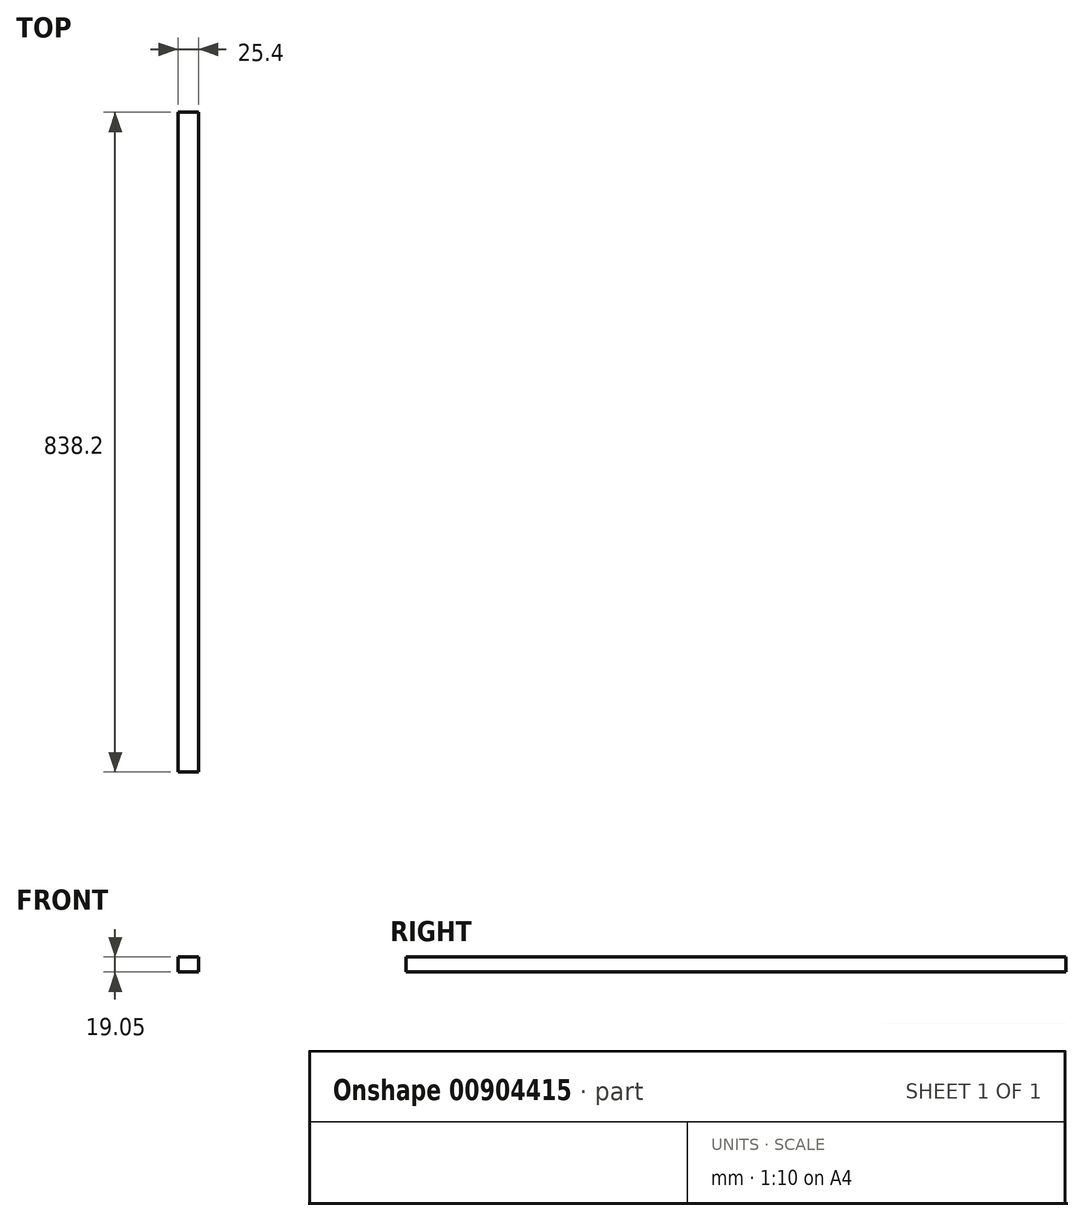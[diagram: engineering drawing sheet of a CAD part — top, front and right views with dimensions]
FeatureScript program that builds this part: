
annotation { "Feature Type Name" : "Feature", "Feature Type Description" : "" }
export const myFeature = defineFeature(function(context is Context, id is Id, definition is map)
    precondition{}
    {
        {
            var Q0;
            Q0=qCreatedBy(makeId("Top.planeOp"),FACE);
            var sketch = newSketch(context, id + "F0", { "sketchPlane" : qUnion([Q0])});
            skLineSegment(sketch, "E0.bottom", {"start": v(0, 0) * mm, "end": v(25.4, 0) * mm});
            skLineSegment(sketch, "E0.top", {"start": v(0, 838.2) * mm, "end": v(25.4, 838.2) * mm});
            skLineSegment(sketch, "E0.left", {"start": v(0, 0) * mm, "end": v(0, 838.2) * mm});
            skLineSegment(sketch, "E0.right", {"start": v(25.4, 0) * mm, "end": v(25.4, 838.2) * mm});
            skSolve(sketch);
        }
        {
            var Q0;
            Q0 = qSketchRegion(id + "F0", true);
            extrude(context, id + "F1", {"entities" : qUnion([Q0]), "depth" : 19.05 * mm, "offsetDistance" : 25.4 * mm});
        }
    });
